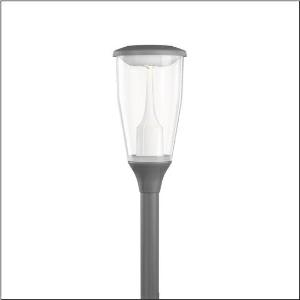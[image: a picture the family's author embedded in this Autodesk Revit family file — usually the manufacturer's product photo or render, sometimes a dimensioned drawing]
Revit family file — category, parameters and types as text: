
# Revit family: dl_11_iq___st1_2a_5xa5575kf14hp00022_6351
name_source: partatom
category: Lighting Fixtures
units: mm (PartAtom-declared; Revit-internal decimal feet)

## family parameters
Cut with Voids When Loaded = No
Host = Face
Light Source = No
Part Type = Normal
Room Calculation Point = No
Round Connector Dimension = Use Diameter
Shared = No

## types (1)
- --- (1 x LED, 5060 lm, 33.6 W, 4000K)
    Apparent Load = 34 VA
    CIE Flux Codes = 33 63 91 94 100
    Color Rendering = 70
    Color Temperature = 4000K
    Default Elevation = 1800 mm
    Description = DL 11 iQ, mast luminaire, Module 540 iQ-SR, primary light control with 3 zone facetted reflector, of plastic, silver coated, highly specular, structured, primary optical cover: cover, of PMMA, transparent, light distribution: ST1.2a, light emission: direct distribution, primary light characteristic: asymmetric, installation type: post-top, LED, High Power LED, light colour: 740, colour temperature: 4000K, control: Street-Remote, Auto-Match, Temp-Guard, Lumen-Switch, Night-Set, Smart-Wire, Light-Fading, Desk-Remote (wireless, voltage-free reading and setting of iQ features in the workshop via application-optimized NFC function/RFID function), optimised constant luminous flux control (CLO 2.0), mains connection: 220..240V, AC, 50/60Hz, connection cable pre-assembled, cable length: 5,5m, wiring characteristics: H07RN-F, 5-core, 1.5mm², start of lifetime: 34W, end of service life: 36W, luminaire housing, upper part, of diecast aluminium, coated, Siteco® metallic grey (DB 702S), spigot size: 76mm (post-top), post-top mast mounting element, of diecast aluminium, coated, Siteco® metallic grey (DB 702S), Module 540 iQ-SR, traffic white (RAL 9016), equipment: Power, protection rating (complete): IP66, insulation class (complete): insulation class II (safety insulation), certification: CE, ENEC, ENEC+, VDE, packaging unit: 1 piece

Light Distribution: ST1.2a
    Height = 665 mm
    Lamp = 1 x LED
    Lamp Light Flux = 5060 lm
    Lamp Power = 33.6 W
    Lamp count = 1
    Length = 334 mm
    Luminous efficacy = 151 lm/W
    Manufacturer = Siteco
    ModVariant = No
    Model = 5XA5575KF14HP00022
    Number of Poles = 1
    OnlyDefault = Yes
    Power Factor = 1
    Product Name = DL 11 iQ | ST1.2a
    Product group = mast luminaire | pylon top
    ProductGroupID = 6100
    Protection Class = Protection class II
    Protection Degree = IP 66
    RLX_Detail_Level = 1
    RLX_Emergency_Light_Flux = 0 lm
    RLX_Emergency_Type = 0
    RLX_Emergency_Type_DB = No
    RlxData = <blob elided: 160989 chars, md5=28987609>
    Socket = socket
    Standby Power = 0 W
    System Light Flux = 5060 lm
    System Power = 34 W
    Type Comments = factory setting: luminous flux: 100 % | dim-lin: 254 | 695 mA
    Type Image = l_1258354.jpg
    URL = http://relux.com
    VarID = @adj_019883
    Voltage = 0 V
    Weight = 0.00 kg
    Width = 0 mm  [stored 0 ft]

note: [stored X ft] marks values corroborated as IEEE doubles in the binary element streams (Revit-internal decimal feet)

## geometry (parser evidence)
native form markers: Blend x4, Sweep x13
no freeform markers — native parametric forms only
